# Revit family: BE_66160_de_DE
name_source: partatom
category: Leuchten
revit_build: Autodesk Revit 2015 (Build: 20150704_0715(x64)
units: mm (PartAtom-declared; Revit-internal decimal feet)

## types (4) — shared parameters
AC/DC = AC/DC
Aktualisierung = 2015-10-23T04:08:04
BEGA_Dummy = Nein
BEGA_IES = Ja
BEGA_Intern = Ja
BEGA_Intern_Konstruktion = Ja
BEGA_Intern_an = Ja
BEGA_Intern_aus = Ja
Befestigungsabstand = 140 mm
Befestigungsbohrung = Ø 4,8 mm
Beschreibung = Deckenaufbau-Tiefstrahler
Beschreibung_Sonderanfertigung = Hier können Sie Informationen zur Sonderanfertigung eintragen.
CE_Konformität = ja
Energieeffizienzklasse = LED A++ - A
Farbfilter = 16777215
Farbtemperaturverschiebung bei Dämpfen der Lampe = <Keine Auswahl>
Farbwiedergabeindex = Ra > 80
Frequenz = 0/50-60 Hz
Hersteller = BEGA
Lampe = LED 34.4 W
Lampenlichtstrom = 4640 lm
Lastklassifizierung = Beleuchtung
Lebensdauerkriterien = L70 = 50.000 h
Leuchtenlichtstrom = 3414 lm
Logo = BEGA_Logo.png
Material_03 = BEGA_Oberfläche_Weiss_matt
Material_06 = BEGA_Oberfläche_Edelstahl_gebürstet
Material_09 = BEGA_Glas_klar
Material_15 = BEGA_Leuchtmedium_matt
Material_19 = BEGA_Dummy_matt
Neigungswinkel = 0.00°
Produktdatenblatt = http://www.bega.de
Scheinlast = 0 VA
Schutzart = IP 65
Schutzklasse = I
Sonderanfertigung = Nein
Spannung = 0 V
Typenbild = 66160.png
URL = http://www.bega.de
zero-valued in all types: Vorgabe-Ansicht

## per-type parameters (varying)
| type | Bestellnummer | Datei für fotometrisches Netz | Farbtemperatur | LED_Modulbezeichnung | M_G | M_W | Modell |
| BEGA_66160_Grafit_K3 | 66160 | BE_66160.IES | 3000 K | 4x LED-0588/830 | Ja | Nein | 66160 |
| BEGA_66160_Grafit_K4 | 66160K4 | BE_66160K4.IES | 4000 K | 4x LED-0588/840 | Ja | Nein | 66160K4 |
| BEGA_66160_Weiß_K3 | 66160W | BE_66160.IES | 3000 K | 4x LED-0588/830 | Nein | Ja | 66160W |
| BEGA_66160_Weiß_K4 | 66160WK4 | BE_66160K4.IES | 4000 K | 4x LED-0588/840 | Nein | Ja | 66160WK4 |

## geometry (parser evidence)
native form markers: Blend x2
no freeform markers — native parametric forms only
